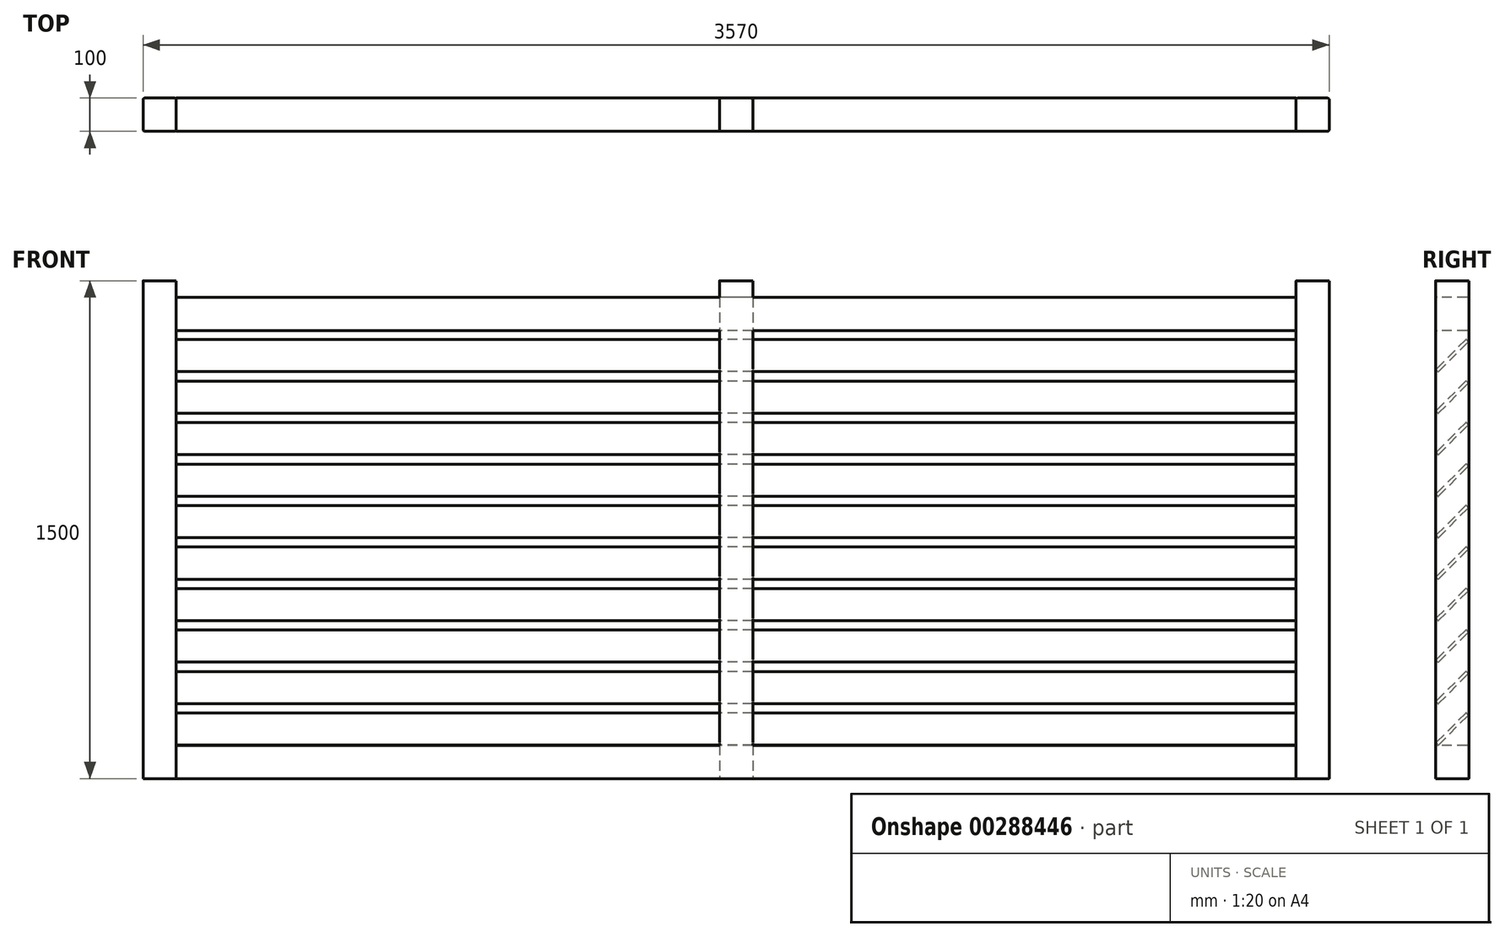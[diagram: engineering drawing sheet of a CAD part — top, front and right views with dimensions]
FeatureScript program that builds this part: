
annotation { "Feature Type Name" : "Feature", "Feature Type Description" : "" }
export const myFeature = defineFeature(function(context is Context, id is Id, definition is map)
    precondition{}
    {
        {
            var Q0;
            Q0=qCreatedBy(makeId("Right.planeOp"),FACE);
            var sketch = newSketch(context, id + "F0", { "sketchPlane" : qUnion([Q0])});
            skLineSegment(sketch, "E0", {"start": v(1.41, 1.41) * mm, "end": v(89.8, 89.8) * mm});
            skLineSegment(sketch, "E1", {"start": v(89.8, 92.63) * mm, "end": v(85.56, 96.87) * mm});
            skLineSegment(sketch, "E2", {"start": v(82.73, 96.87) * mm, "end": v(-5.66, 8.49) * mm});
            skLineSegment(sketch, "E3", {"start": v(-5.66, 5.66) * mm, "end": v(-1.41, 1.41) * mm});
            skPoint(sketch, "E4.visualSharp", {"position": v(84.15, 98.29) * mm});
            skArc(sketch, "E4.filletArc", {"start": v(85.56, 96.87) * mm, "mid": v(84.15, 97.46) * mm, "end": v(82.73, 96.87) * mm});
            skPoint(sketch, "E5.visualSharp", {"position": v(91.22, 91.22) * mm});
            skArc(sketch, "E5.filletArc", {"start": v(89.8, 89.8) * mm, "mid": v(90.39, 91.22) * mm, "end": v(89.8, 92.63) * mm});
            skPoint(sketch, "E6.visualSharp", {"position": v(0, 0) * mm});
            skArc(sketch, "E6.filletArc", {"start": v(-1.41, 1.41) * mm, "mid": v(0, 0.83) * mm, "end": v(1.41, 1.41) * mm});
            skPoint(sketch, "E7.visualSharp", {"position": v(-7.07, 7.07) * mm});
            skArc(sketch, "E7.filletArc", {"start": v(-5.66, 8.49) * mm, "mid": v(-6.24, 7.07) * mm, "end": v(-5.66, 5.66) * mm});
            skLineSegment(sketch, "E8.0.1.0", {"start": v(1.41, 126.41) * mm, "end": v(89.8, 214.8) * mm});
            skLineSegment(sketch, "E8.0.1.1", {"start": v(82.73, 221.87) * mm, "end": v(-5.66, 133.49) * mm});
            skPoint(sketch, "E8.0.1.2", {"position": v(84.15, 223.29) * mm});
            skPoint(sketch, "E8.0.1.3", {"position": v(91.22, 216.22) * mm});
            skPoint(sketch, "E8.0.1.4", {"position": v(-7.07, 132.07) * mm});
            skPoint(sketch, "E8.0.1.5", {"position": v(0, 125) * mm});
            skArc(sketch, "E8.0.1.6", {"start": v(89.8, 214.8) * mm, "mid": v(90.39, 216.22) * mm, "end": v(89.8, 217.63) * mm});
            skArc(sketch, "E8.0.1.7", {"start": v(-1.41, 126.41) * mm, "mid": v(0, 125.83) * mm, "end": v(1.41, 126.41) * mm});
            skArc(sketch, "E8.0.1.8", {"start": v(85.56, 221.87) * mm, "mid": v(84.15, 222.46) * mm, "end": v(82.73, 221.87) * mm});
            skLineSegment(sketch, "E8.0.1.9", {"start": v(-5.66, 130.66) * mm, "end": v(-1.41, 126.41) * mm});
            skArc(sketch, "E8.0.1.10", {"start": v(-5.66, 133.49) * mm, "mid": v(-6.24, 132.07) * mm, "end": v(-5.66, 130.66) * mm});
            skLineSegment(sketch, "E8.0.1.11", {"start": v(89.8, 217.63) * mm, "end": v(85.56, 221.87) * mm});
            skLineSegment(sketch, "E8.0.2.0", {"start": v(1.41, 251.41) * mm, "end": v(89.8, 339.8) * mm});
            skLineSegment(sketch, "E8.0.2.1", {"start": v(82.73, 346.87) * mm, "end": v(-5.66, 258.49) * mm});
            skPoint(sketch, "E8.0.2.2", {"position": v(84.15, 348.29) * mm});
            skPoint(sketch, "E8.0.2.3", {"position": v(91.22, 341.22) * mm});
            skPoint(sketch, "E8.0.2.4", {"position": v(-7.07, 257.07) * mm});
            skPoint(sketch, "E8.0.2.5", {"position": v(0, 250) * mm});
            skArc(sketch, "E8.0.2.6", {"start": v(89.8, 339.8) * mm, "mid": v(90.39, 341.22) * mm, "end": v(89.8, 342.63) * mm});
            skArc(sketch, "E8.0.2.7", {"start": v(-1.41, 251.41) * mm, "mid": v(0, 250.83) * mm, "end": v(1.41, 251.41) * mm});
            skArc(sketch, "E8.0.2.8", {"start": v(85.56, 346.87) * mm, "mid": v(84.15, 347.46) * mm, "end": v(82.73, 346.87) * mm});
            skLineSegment(sketch, "E8.0.2.9", {"start": v(-5.66, 255.66) * mm, "end": v(-1.41, 251.41) * mm});
            skArc(sketch, "E8.0.2.10", {"start": v(-5.66, 258.49) * mm, "mid": v(-6.24, 257.07) * mm, "end": v(-5.66, 255.66) * mm});
            skLineSegment(sketch, "E8.0.2.11", {"start": v(89.8, 342.63) * mm, "end": v(85.56, 346.87) * mm});
            skLineSegment(sketch, "E8.0.3.0", {"start": v(1.41, 376.41) * mm, "end": v(89.8, 464.8) * mm});
            skLineSegment(sketch, "E8.0.3.1", {"start": v(82.73, 471.87) * mm, "end": v(-5.66, 383.49) * mm});
            skPoint(sketch, "E8.0.3.2", {"position": v(84.15, 473.29) * mm});
            skPoint(sketch, "E8.0.3.3", {"position": v(91.22, 466.22) * mm});
            skPoint(sketch, "E8.0.3.4", {"position": v(-7.07, 382.07) * mm});
            skPoint(sketch, "E8.0.3.5", {"position": v(0, 375) * mm});
            skArc(sketch, "E8.0.3.6", {"start": v(89.8, 464.8) * mm, "mid": v(90.39, 466.22) * mm, "end": v(89.8, 467.63) * mm});
            skArc(sketch, "E8.0.3.7", {"start": v(-1.41, 376.41) * mm, "mid": v(0, 375.83) * mm, "end": v(1.41, 376.41) * mm});
            skArc(sketch, "E8.0.3.8", {"start": v(85.56, 471.87) * mm, "mid": v(84.15, 472.46) * mm, "end": v(82.73, 471.87) * mm});
            skLineSegment(sketch, "E8.0.3.9", {"start": v(-5.66, 380.66) * mm, "end": v(-1.41, 376.41) * mm});
            skArc(sketch, "E8.0.3.10", {"start": v(-5.66, 383.49) * mm, "mid": v(-6.24, 382.07) * mm, "end": v(-5.66, 380.66) * mm});
            skLineSegment(sketch, "E8.0.3.11", {"start": v(89.8, 467.63) * mm, "end": v(85.56, 471.87) * mm});
            skLineSegment(sketch, "E8.0.4.0", {"start": v(1.41, 501.41) * mm, "end": v(89.8, 589.8) * mm});
            skLineSegment(sketch, "E8.0.4.1", {"start": v(82.73, 596.87) * mm, "end": v(-5.66, 508.49) * mm});
            skPoint(sketch, "E8.0.4.2", {"position": v(84.15, 598.29) * mm});
            skPoint(sketch, "E8.0.4.3", {"position": v(91.22, 591.22) * mm});
            skPoint(sketch, "E8.0.4.4", {"position": v(-7.07, 507.07) * mm});
            skPoint(sketch, "E8.0.4.5", {"position": v(0, 500) * mm});
            skArc(sketch, "E8.0.4.6", {"start": v(89.8, 589.8) * mm, "mid": v(90.39, 591.22) * mm, "end": v(89.8, 592.63) * mm});
            skArc(sketch, "E8.0.4.7", {"start": v(-1.41, 501.41) * mm, "mid": v(0, 500.83) * mm, "end": v(1.41, 501.41) * mm});
            skArc(sketch, "E8.0.4.8", {"start": v(85.56, 596.87) * mm, "mid": v(84.15, 597.46) * mm, "end": v(82.73, 596.87) * mm});
            skLineSegment(sketch, "E8.0.4.9", {"start": v(-5.66, 505.66) * mm, "end": v(-1.41, 501.41) * mm});
            skArc(sketch, "E8.0.4.10", {"start": v(-5.66, 508.49) * mm, "mid": v(-6.24, 507.07) * mm, "end": v(-5.66, 505.66) * mm});
            skLineSegment(sketch, "E8.0.4.11", {"start": v(89.8, 592.63) * mm, "end": v(85.56, 596.87) * mm});
            skLineSegment(sketch, "E8.0.5.0", {"start": v(1.41, 626.41) * mm, "end": v(89.8, 714.8) * mm});
            skLineSegment(sketch, "E8.0.5.1", {"start": v(82.73, 721.87) * mm, "end": v(-5.66, 633.49) * mm});
            skPoint(sketch, "E8.0.5.2", {"position": v(84.15, 723.29) * mm});
            skPoint(sketch, "E8.0.5.3", {"position": v(91.22, 716.22) * mm});
            skPoint(sketch, "E8.0.5.4", {"position": v(-7.07, 632.07) * mm});
            skPoint(sketch, "E8.0.5.5", {"position": v(0, 625) * mm});
            skArc(sketch, "E8.0.5.6", {"start": v(89.8, 714.8) * mm, "mid": v(90.39, 716.22) * mm, "end": v(89.8, 717.63) * mm});
            skArc(sketch, "E8.0.5.7", {"start": v(-1.41, 626.41) * mm, "mid": v(0, 625.83) * mm, "end": v(1.41, 626.41) * mm});
            skArc(sketch, "E8.0.5.8", {"start": v(85.56, 721.87) * mm, "mid": v(84.15, 722.46) * mm, "end": v(82.73, 721.87) * mm});
            skLineSegment(sketch, "E8.0.5.9", {"start": v(-5.66, 630.66) * mm, "end": v(-1.41, 626.41) * mm});
            skArc(sketch, "E8.0.5.10", {"start": v(-5.66, 633.49) * mm, "mid": v(-6.24, 632.07) * mm, "end": v(-5.66, 630.66) * mm});
            skLineSegment(sketch, "E8.0.5.11", {"start": v(89.8, 717.63) * mm, "end": v(85.56, 721.87) * mm});
            skLineSegment(sketch, "E8.0.6.0", {"start": v(1.41, 751.41) * mm, "end": v(89.8, 839.8) * mm});
            skLineSegment(sketch, "E8.0.6.1", {"start": v(82.73, 846.87) * mm, "end": v(-5.66, 758.49) * mm});
            skPoint(sketch, "E8.0.6.2", {"position": v(84.15, 848.29) * mm});
            skPoint(sketch, "E8.0.6.3", {"position": v(91.22, 841.22) * mm});
            skPoint(sketch, "E8.0.6.4", {"position": v(-7.07, 757.07) * mm});
            skPoint(sketch, "E8.0.6.5", {"position": v(0, 750) * mm});
            skArc(sketch, "E8.0.6.6", {"start": v(89.8, 839.8) * mm, "mid": v(90.39, 841.22) * mm, "end": v(89.8, 842.63) * mm});
            skArc(sketch, "E8.0.6.7", {"start": v(-1.41, 751.41) * mm, "mid": v(0, 750.83) * mm, "end": v(1.41, 751.41) * mm});
            skArc(sketch, "E8.0.6.8", {"start": v(85.56, 846.87) * mm, "mid": v(84.15, 847.46) * mm, "end": v(82.73, 846.87) * mm});
            skLineSegment(sketch, "E8.0.6.9", {"start": v(-5.66, 755.66) * mm, "end": v(-1.41, 751.41) * mm});
            skArc(sketch, "E8.0.6.10", {"start": v(-5.66, 758.49) * mm, "mid": v(-6.24, 757.07) * mm, "end": v(-5.66, 755.66) * mm});
            skLineSegment(sketch, "E8.0.6.11", {"start": v(89.8, 842.63) * mm, "end": v(85.56, 846.87) * mm});
            skLineSegment(sketch, "E8.0.7.0", {"start": v(1.41, 876.41) * mm, "end": v(89.8, 964.8) * mm});
            skLineSegment(sketch, "E8.0.7.1", {"start": v(82.73, 971.87) * mm, "end": v(-5.66, 883.49) * mm});
            skPoint(sketch, "E8.0.7.2", {"position": v(84.15, 973.29) * mm});
            skPoint(sketch, "E8.0.7.3", {"position": v(91.22, 966.22) * mm});
            skPoint(sketch, "E8.0.7.4", {"position": v(-7.07, 882.07) * mm});
            skPoint(sketch, "E8.0.7.5", {"position": v(0, 875) * mm});
            skArc(sketch, "E8.0.7.6", {"start": v(89.8, 964.8) * mm, "mid": v(90.39, 966.22) * mm, "end": v(89.8, 967.63) * mm});
            skArc(sketch, "E8.0.7.7", {"start": v(-1.41, 876.41) * mm, "mid": v(0, 875.83) * mm, "end": v(1.41, 876.41) * mm});
            skArc(sketch, "E8.0.7.8", {"start": v(85.56, 971.87) * mm, "mid": v(84.15, 972.46) * mm, "end": v(82.73, 971.87) * mm});
            skLineSegment(sketch, "E8.0.7.9", {"start": v(-5.66, 880.66) * mm, "end": v(-1.41, 876.41) * mm});
            skArc(sketch, "E8.0.7.10", {"start": v(-5.66, 883.49) * mm, "mid": v(-6.24, 882.07) * mm, "end": v(-5.66, 880.66) * mm});
            skLineSegment(sketch, "E8.0.7.11", {"start": v(89.8, 967.63) * mm, "end": v(85.56, 971.87) * mm});
            skLineSegment(sketch, "E8.direction1", {"start": v(0, 0) * mm, "end": v(25, 0) * mm, "construction": true});
            skLineSegment(sketch, "E8.direction2", {"start": v(0, 0) * mm, "end": v(0, 125) * mm, "construction": true});
            skLineSegment(sketch, "E9.0.0.8", {"start": v(1.41, 1001.41) * mm, "end": v(89.8, 1089.8) * mm});
            skLineSegment(sketch, "E9.3.0.8", {"start": v(82.73, 1096.87) * mm, "end": v(-5.66, 1008.49) * mm});
            skPoint(sketch, "E9.6.0.8", {"position": v(84.15, 1098.29) * mm});
            skPoint(sketch, "E9.7.0.8", {"position": v(91.22, 1091.22) * mm});
            skPoint(sketch, "E9.8.0.8", {"position": v(-7.07, 1007.07) * mm});
            skPoint(sketch, "E9.9.0.8", {"position": v(0, 1000) * mm});
            skArc(sketch, "E9.10.0.8", {"start": v(89.8, 1089.8) * mm, "mid": v(90.39, 1091.22) * mm, "end": v(89.8, 1092.63) * mm});
            skArc(sketch, "E9.14.0.8", {"start": v(-1.41, 1001.41) * mm, "mid": v(0, 1000.83) * mm, "end": v(1.41, 1001.41) * mm});
            skArc(sketch, "E9.18.0.8", {"start": v(85.56, 1096.87) * mm, "mid": v(84.15, 1097.46) * mm, "end": v(82.73, 1096.87) * mm});
            skLineSegment(sketch, "E9.22.0.8", {"start": v(-5.66, 1005.66) * mm, "end": v(-1.41, 1001.41) * mm});
            skArc(sketch, "E9.25.0.8", {"start": v(-5.66, 1008.49) * mm, "mid": v(-6.24, 1007.07) * mm, "end": v(-5.66, 1005.66) * mm});
            skLineSegment(sketch, "E9.29.0.8", {"start": v(89.8, 1092.63) * mm, "end": v(85.56, 1096.87) * mm});
            skLineSegment(sketch, "E9.0.0.9", {"start": v(1.41, 1126.41) * mm, "end": v(89.8, 1214.8) * mm});
            skLineSegment(sketch, "E9.3.0.9", {"start": v(82.73, 1221.87) * mm, "end": v(-5.66, 1133.49) * mm});
            skPoint(sketch, "E9.6.0.9", {"position": v(84.15, 1223.29) * mm});
            skPoint(sketch, "E9.7.0.9", {"position": v(91.22, 1216.22) * mm});
            skPoint(sketch, "E9.8.0.9", {"position": v(-7.07, 1132.07) * mm});
            skPoint(sketch, "E9.9.0.9", {"position": v(0, 1125) * mm});
            skArc(sketch, "E9.10.0.9", {"start": v(89.8, 1214.8) * mm, "mid": v(90.39, 1216.22) * mm, "end": v(89.8, 1217.63) * mm});
            skArc(sketch, "E9.14.0.9", {"start": v(-1.41, 1126.41) * mm, "mid": v(0, 1125.83) * mm, "end": v(1.41, 1126.41) * mm});
            skArc(sketch, "E9.18.0.9", {"start": v(85.56, 1221.87) * mm, "mid": v(84.15, 1222.46) * mm, "end": v(82.73, 1221.87) * mm});
            skLineSegment(sketch, "E9.22.0.9", {"start": v(-5.66, 1130.66) * mm, "end": v(-1.41, 1126.41) * mm});
            skArc(sketch, "E9.25.0.9", {"start": v(-5.66, 1133.49) * mm, "mid": v(-6.24, 1132.07) * mm, "end": v(-5.66, 1130.66) * mm});
            skLineSegment(sketch, "E9.29.0.9", {"start": v(89.8, 1217.63) * mm, "end": v(85.56, 1221.87) * mm});
            skSolve(sketch);
        }
        {
            var Q0;
            Q0=makeQuery(id+"F0.imprint","IMPRINT",FACE,{"disambiguationData":[TD([[makeQuery(id+"F0.imprint","IMPRINT",EDGE,{"derivedFrom":sQuery(id+"F0.wireOp",EDGE,"E0")}),1.0]])]});
            var Q1;
            Q1=makeQuery(id+"F0.imprint","IMPRINT",FACE,{"disambiguationData":[TD([[makeQuery(id+"F0.imprint","IMPRINT",EDGE,{"derivedFrom":sQuery(id+"F0.wireOp",EDGE,"E8.0.1.0")}),1.0]])]});
            var Q2;
            Q2=makeQuery(id+"F0.imprint","IMPRINT",FACE,{"disambiguationData":[TD([[makeQuery(id+"F0.imprint","IMPRINT",EDGE,{"derivedFrom":sQuery(id+"F0.wireOp",EDGE,"E8.0.2.0")}),1.0]])]});
            var Q3;
            Q3=makeQuery(id+"F0.imprint","IMPRINT",FACE,{"disambiguationData":[TD([[makeQuery(id+"F0.imprint","IMPRINT",EDGE,{"derivedFrom":sQuery(id+"F0.wireOp",EDGE,"E8.0.3.0")}),1.0]])]});
            var Q4;
            Q4=makeQuery(id+"F0.imprint","IMPRINT",FACE,{"disambiguationData":[TD([[makeQuery(id+"F0.imprint","IMPRINT",EDGE,{"derivedFrom":sQuery(id+"F0.wireOp",EDGE,"E8.0.4.0")}),1.0]])]});
            var Q5;
            Q5=makeQuery(id+"F0.imprint","IMPRINT",FACE,{"disambiguationData":[TD([[makeQuery(id+"F0.imprint","IMPRINT",EDGE,{"derivedFrom":sQuery(id+"F0.wireOp",EDGE,"E8.0.5.0")}),1.0]])]});
            var Q6;
            Q6=makeQuery(id+"F0.imprint","IMPRINT",FACE,{"disambiguationData":[TD([[makeQuery(id+"F0.imprint","IMPRINT",EDGE,{"derivedFrom":sQuery(id+"F0.wireOp",EDGE,"E8.0.6.0")}),1.0]])]});
            var Q7;
            Q7=makeQuery(id+"F0.imprint","IMPRINT",FACE,{"disambiguationData":[TD([[makeQuery(id+"F0.imprint","IMPRINT",EDGE,{"derivedFrom":sQuery(id+"F0.wireOp",EDGE,"E8.0.7.0")}),1.0]])]});
            var Q8;
            Q8=makeQuery(id+"F0.imprint","IMPRINT",FACE,{"disambiguationData":[TD([[makeQuery(id+"F0.imprint","IMPRINT",EDGE,{"derivedFrom":sQuery(id+"F0.wireOp",EDGE,"E8.0.8.0")}),1.0]])]});
            var Q9;
            Q9=makeQuery(id+"F0.imprint","IMPRINT",FACE,{"disambiguationData":[TD([[makeQuery(id+"F0.imprint","IMPRINT",EDGE,{"derivedFrom":sQuery(id+"F0.wireOp",EDGE,"E8.0.9.0")}),1.0]])]});
            var Q10;
            Q10=makeQuery(id+"F0.imprint","IMPRINT",FACE,{"disambiguationData":[TD([[makeQuery(id+"F0.imprint","IMPRINT",EDGE,{"derivedFrom":sQuery(id+"F0.wireOp",EDGE,"E8.0.10.0")}),1.0]])]});
            var Q11;
            Q11=makeQuery(id+"F0.imprint","IMPRINT",FACE,{"disambiguationData":[TD([[makeQuery(id+"F0.imprint","IMPRINT",EDGE,{"derivedFrom":sQuery(id+"F0.wireOp",EDGE,"E8.0.28.0")}),1.0]])]});
            var Q12;
            Q12=makeQuery(id+"F0.imprint","IMPRINT",FACE,{"disambiguationData":[TD([[makeQuery(id+"F0.imprint","IMPRINT",EDGE,{"derivedFrom":sQuery(id+"F0.wireOp",EDGE,"E8.0.27.0")}),1.0]])]});
            var Q13;
            Q13=makeQuery(id+"F0.imprint","IMPRINT",FACE,{"disambiguationData":[TD([[makeQuery(id+"F0.imprint","IMPRINT",EDGE,{"derivedFrom":sQuery(id+"F0.wireOp",EDGE,"E8.0.26.0")}),1.0]])]});
            var Q14;
            Q14=makeQuery(id+"F0.imprint","IMPRINT",FACE,{"disambiguationData":[TD([[makeQuery(id+"F0.imprint","IMPRINT",EDGE,{"derivedFrom":sQuery(id+"F0.wireOp",EDGE,"E8.0.29.0")}),1.0]])]});
            var Q15;
            Q15=makeQuery(id+"F0.imprint","IMPRINT",FACE,{"disambiguationData":[TD([[makeQuery(id+"F0.imprint","IMPRINT",EDGE,{"derivedFrom":sQuery(id+"F0.wireOp",EDGE,"E8.0.16.0")}),1.0]])]});
            var Q16;
            Q16=makeQuery(id+"F0.imprint","IMPRINT",FACE,{"disambiguationData":[TD([[makeQuery(id+"F0.imprint","IMPRINT",EDGE,{"derivedFrom":sQuery(id+"F0.wireOp",EDGE,"E8.0.17.0")}),1.0]])]});
            var Q17;
            Q17=makeQuery(id+"F0.imprint","IMPRINT",FACE,{"disambiguationData":[TD([[makeQuery(id+"F0.imprint","IMPRINT",EDGE,{"derivedFrom":sQuery(id+"F0.wireOp",EDGE,"E8.0.18.0")}),1.0]])]});
            var Q18;
            Q18=makeQuery(id+"F0.imprint","IMPRINT",FACE,{"disambiguationData":[TD([[makeQuery(id+"F0.imprint","IMPRINT",EDGE,{"derivedFrom":sQuery(id+"F0.wireOp",EDGE,"E8.0.19.0")}),1.0]])]});
            var Q19;
            Q19=makeQuery(id+"F0.imprint","IMPRINT",FACE,{"disambiguationData":[TD([[makeQuery(id+"F0.imprint","IMPRINT",EDGE,{"derivedFrom":sQuery(id+"F0.wireOp",EDGE,"E8.0.20.0")}),1.0]])]});
            var Q20;
            Q20=makeQuery(id+"F0.imprint","IMPRINT",FACE,{"disambiguationData":[TD([[makeQuery(id+"F0.imprint","IMPRINT",EDGE,{"derivedFrom":sQuery(id+"F0.wireOp",EDGE,"E8.0.21.0")}),1.0]])]});
            var Q21;
            Q21=makeQuery(id+"F0.imprint","IMPRINT",FACE,{"disambiguationData":[TD([[makeQuery(id+"F0.imprint","IMPRINT",EDGE,{"derivedFrom":sQuery(id+"F0.wireOp",EDGE,"E8.0.22.0")}),1.0]])]});
            var Q22;
            Q22=makeQuery(id+"F0.imprint","IMPRINT",FACE,{"disambiguationData":[TD([[makeQuery(id+"F0.imprint","IMPRINT",EDGE,{"derivedFrom":sQuery(id+"F0.wireOp",EDGE,"E8.0.15.0")}),1.0]])]});
            var Q23;
            Q23=makeQuery(id+"F0.imprint","IMPRINT",FACE,{"disambiguationData":[TD([[makeQuery(id+"F0.imprint","IMPRINT",EDGE,{"derivedFrom":sQuery(id+"F0.wireOp",EDGE,"E8.0.13.0")}),1.0]])]});
            var Q24;
            Q24=makeQuery(id+"F0.imprint","IMPRINT",FACE,{"disambiguationData":[TD([[makeQuery(id+"F0.imprint","IMPRINT",EDGE,{"derivedFrom":sQuery(id+"F0.wireOp",EDGE,"E8.0.14.0")}),1.0]])]});
            var Q25;
            Q25=makeQuery(id+"F0.imprint","IMPRINT",FACE,{"disambiguationData":[TD([[makeQuery(id+"F0.imprint","IMPRINT",EDGE,{"derivedFrom":sQuery(id+"F0.wireOp",EDGE,"E8.0.11.0")}),1.0]])]});
            var Q26;
            Q26=makeQuery(id+"F0.imprint","IMPRINT",FACE,{"disambiguationData":[TD([[makeQuery(id+"F0.imprint","IMPRINT",EDGE,{"derivedFrom":sQuery(id+"F0.wireOp",EDGE,"E8.0.12.0")}),1.0]])]});
            var Q27;
            Q27=makeQuery(id+"F0.imprint","IMPRINT",FACE,{"disambiguationData":[TD([[makeQuery(id+"F0.imprint","IMPRINT",EDGE,{"derivedFrom":sQuery(id+"F0.wireOp",EDGE,"E8.0.23.0")}),1.0]])]});
            var Q28;
            Q28=makeQuery(id+"F0.imprint","IMPRINT",FACE,{"disambiguationData":[TD([[makeQuery(id+"F0.imprint","IMPRINT",EDGE,{"derivedFrom":sQuery(id+"F0.wireOp",EDGE,"E8.0.24.0")}),1.0]])]});
            var Q29;
            Q29=makeQuery(id+"F0.imprint","IMPRINT",FACE,{"disambiguationData":[TD([[makeQuery(id+"F0.imprint","IMPRINT",EDGE,{"derivedFrom":sQuery(id+"F0.wireOp",EDGE,"E8.0.25.0")}),1.0]])]});
            var Q30;
            Q30=makeQuery(id+"F0.imprint","IMPRINT",FACE,{"disambiguationData":[TD([[makeQuery(id+"F0.imprint","IMPRINT",EDGE,{"derivedFrom":sQuery(id+"F0.wireOp",EDGE,"E9.0.0.8")}),1.0]])]});
            var Q31;
            Q31=makeQuery(id+"F0.imprint","IMPRINT",FACE,{"disambiguationData":[TD([[makeQuery(id+"F0.imprint","IMPRINT",EDGE,{"derivedFrom":sQuery(id+"F0.wireOp",EDGE,"E9.0.0.9")}),1.0]])]});
            var Q32;
            Q32=makeQuery(id+"F0.imprint","IMPRINT",FACE,{"disambiguationData":[TD([[makeQuery(id+"F0.imprint","IMPRINT",EDGE,{"derivedFrom":sQuery(id+"F0.wireOp",EDGE,"E9.0.0.10")}),1.0]])]});
            var Q33;
            Q33=makeQuery(id+"F0.imprint","IMPRINT",FACE,{"disambiguationData":[TD([[makeQuery(id+"F0.imprint","IMPRINT",EDGE,{"derivedFrom":sQuery(id+"F0.wireOp",EDGE,"E9.0.0.11")}),1.0]])]});
            extrude(context, id + "F1", {"entities" : qUnion([Q0, Q1, Q2, Q3, Q4, Q5, Q6, Q7, Q8, Q9, Q10, Q11, Q12, Q13, Q14, Q15, Q16, Q17, Q18, Q19, Q20, Q21, Q22, Q23, Q24, Q25, Q26, Q27, Q28, Q29, Q30, Q31, Q32, Q33]), "depth" : 3370 * mm});
        }
        {
            var Q0;
            Q0=qCreatedBy(makeId("Top.planeOp"),FACE);
            var sketch = newSketch(context, id + "F2", { "sketchPlane" : qUnion([Q0])});
            skLineSegment(sketch, "E10.bottom", {"start": v(-5, -8) * mm, "end": v(-95, -8) * mm});
            skLineSegment(sketch, "E10.top", {"start": v(-5, 92) * mm, "end": v(-95, 92) * mm});
            skLineSegment(sketch, "E10.left", {"start": v(0, -3) * mm, "end": v(0, 87) * mm});
            skLineSegment(sketch, "E10.right", {"start": v(-100, -3) * mm, "end": v(-100, 87) * mm});
            skPoint(sketch, "E11.visualSharp", {"position": v(-100, 92) * mm});
            skArc(sketch, "E11.filletArc", {"start": v(-95, 92) * mm, "mid": v(-98.54, 90.54) * mm, "end": v(-100, 87) * mm});
            skPoint(sketch, "E12.visualSharp", {"position": v(0, 92) * mm});
            skArc(sketch, "E12.filletArc", {"start": v(0, 87) * mm, "mid": v(-1.46, 90.54) * mm, "end": v(-5, 92) * mm});
            skPoint(sketch, "E13.visualSharp", {"position": v(0, -8) * mm});
            skArc(sketch, "E13.filletArc", {"start": v(-5, -8) * mm, "mid": v(-1.46, -6.54) * mm, "end": v(0, -3) * mm});
            skPoint(sketch, "E14.visualSharp", {"position": v(-100, -8) * mm});
            skArc(sketch, "E14.filletArc", {"start": v(-100, -3) * mm, "mid": v(-98.54, -6.54) * mm, "end": v(-95, -8) * mm});
            skLineSegment(sketch, "E15.1.0.0", {"start": v(1635, -3) * mm, "end": v(1635, 87) * mm});
            skLineSegment(sketch, "E15.1.0.1", {"start": v(1735, -3) * mm, "end": v(1735, 87) * mm});
            skLineSegment(sketch, "E15.1.0.2", {"start": v(1730, -8) * mm, "end": v(1640, -8) * mm});
            skLineSegment(sketch, "E15.1.0.3", {"start": v(1730, 92) * mm, "end": v(1640, 92) * mm});
            skPoint(sketch, "E15.1.0.4", {"position": v(1635, 92) * mm});
            skPoint(sketch, "E15.1.0.5", {"position": v(1635, -8) * mm});
            skPoint(sketch, "E15.1.0.6", {"position": v(1735, 92) * mm});
            skPoint(sketch, "E15.1.0.7", {"position": v(1735, -8) * mm});
            skArc(sketch, "E15.1.0.8", {"start": v(1635, -3) * mm, "mid": v(1636.46, -6.54) * mm, "end": v(1640, -8) * mm});
            skArc(sketch, "E15.1.0.9", {"start": v(1735, 87) * mm, "mid": v(1733.54, 90.54) * mm, "end": v(1730, 92) * mm});
            skArc(sketch, "E15.1.0.10", {"start": v(1730, -8) * mm, "mid": v(1733.54, -6.54) * mm, "end": v(1735, -3) * mm});
            skArc(sketch, "E15.1.0.11", {"start": v(1640, 92) * mm, "mid": v(1636.46, 90.54) * mm, "end": v(1635, 87) * mm});
            skLineSegment(sketch, "E15.direction1", {"start": v(-100, -8) * mm, "end": v(1635, -8) * mm, "construction": true});
            skLineSegment(sketch, "E16.0.2.0", {"start": v(3370, -3) * mm, "end": v(3370, 87) * mm});
            skLineSegment(sketch, "E16.3.2.0", {"start": v(3470, -3) * mm, "end": v(3470, 87) * mm});
            skLineSegment(sketch, "E16.6.2.0", {"start": v(3465, -8) * mm, "end": v(3375, -8) * mm});
            skLineSegment(sketch, "E16.9.2.0", {"start": v(3465, 92) * mm, "end": v(3375, 92) * mm});
            skPoint(sketch, "E16.12.2.0", {"position": v(3370, 92) * mm});
            skPoint(sketch, "E16.13.2.0", {"position": v(3370, -8) * mm});
            skPoint(sketch, "E16.14.2.0", {"position": v(3470, 92) * mm});
            skPoint(sketch, "E16.15.2.0", {"position": v(3470, -8) * mm});
            skArc(sketch, "E16.16.2.0", {"start": v(3370, -3) * mm, "mid": v(3371.46, -6.54) * mm, "end": v(3375, -8) * mm});
            skArc(sketch, "E16.20.2.0", {"start": v(3470, 87) * mm, "mid": v(3468.54, 90.54) * mm, "end": v(3465, 92) * mm});
            skArc(sketch, "E16.24.2.0", {"start": v(3465, -8) * mm, "mid": v(3468.54, -6.54) * mm, "end": v(3470, -3) * mm});
            skArc(sketch, "E16.28.2.0", {"start": v(3375, 92) * mm, "mid": v(3371.46, 90.54) * mm, "end": v(3370, 87) * mm});
            skSolve(sketch);
        }
        {
            var Q0;
            Q0=makeQuery(id+"F2.imprint","IMPRINT",FACE,{"disambiguationData":[TD([[makeQuery(id+"F2.imprint","IMPRINT",EDGE,{"derivedFrom":sQuery(id+"F2.wireOp",EDGE,"E10.bottom")}),-1.0]])]});
            var Q1;
            Q1=makeQuery(id+"F2.imprint","IMPRINT",FACE,{"disambiguationData":[TD([[makeQuery(id+"F2.imprint","IMPRINT",EDGE,{"derivedFrom":sQuery(id+"F2.wireOp",EDGE,"E15.1.0.0")}),-1.0]])]});
            var Q2;
            Q2=makeQuery(id+"F2.imprint","IMPRINT",FACE,{"disambiguationData":[TD([[makeQuery(id+"F2.imprint","IMPRINT",EDGE,{"derivedFrom":sQuery(id+"F2.wireOp",EDGE,"E16.0.2.0")}),-1.0]])]});
            extrude(context, id + "F3", {"entities" : qUnion([Q0, Q1, Q2]), "depth" : 1400 * mm, "hasSecondDirection" : true, "secondDirectionOppositeDirection" : true, "secondDirectionDepth" : 100 * mm});
        }
        {
            var Q0;
            Q0=makeQuery(id+"F3.opExtrude","SWEPT_FACE",FACE,{"disambiguationData":[OSD([sQuery(id+"F2.wireOp",EDGE,"E10.left")])]});
            var sketch = newSketch(context, id + "F4", { "sketchPlane" : qUnion([Q0])});
            skLineSegment(sketch, "E17.bottom", {"start": v(87, -100) * mm, "end": v(-3, -100) * mm});
            skLineSegment(sketch, "E17.top", {"start": v(87, 0) * mm, "end": v(-3, 0) * mm});
            skLineSegment(sketch, "E17.left", {"start": v(92, -95) * mm, "end": v(92, -5) * mm});
            skLineSegment(sketch, "E17.right", {"start": v(-8, -95) * mm, "end": v(-8, -5) * mm});
            skPoint(sketch, "E18.visualSharp", {"position": v(92, 0) * mm});
            skArc(sketch, "E18.filletArc", {"start": v(92, -5) * mm, "mid": v(90.54, -1.46) * mm, "end": v(87, 0) * mm});
            skPoint(sketch, "E19.visualSharp", {"position": v(92, -100) * mm});
            skArc(sketch, "E19.filletArc", {"start": v(87, -100) * mm, "mid": v(90.54, -98.54) * mm, "end": v(92, -95) * mm});
            skPoint(sketch, "E20.visualSharp", {"position": v(-8, -100) * mm});
            skArc(sketch, "E20.filletArc", {"start": v(-8, -95) * mm, "mid": v(-6.54, -98.54) * mm, "end": v(-3, -100) * mm});
            skPoint(sketch, "E21.visualSharp", {"position": v(-8, 0) * mm});
            skArc(sketch, "E21.filletArc", {"start": v(-3, 0) * mm, "mid": v(-6.54, -1.46) * mm, "end": v(-8, -5) * mm});
            skLineSegment(sketch, "E22.0.1.0", {"start": v(87, 1250) * mm, "end": v(-3, 1250) * mm});
            skPoint(sketch, "E22.0.1.1", {"position": v(-8, 1250) * mm});
            skPoint(sketch, "E22.0.1.2", {"position": v(-8, 1350) * mm});
            skLineSegment(sketch, "E22.0.1.3", {"start": v(-8, 1255) * mm, "end": v(-8, 1345) * mm});
            skPoint(sketch, "E22.0.1.4", {"position": v(92, 1350) * mm});
            skPoint(sketch, "E22.0.1.5", {"position": v(92, 1250) * mm});
            skLineSegment(sketch, "E22.0.1.6", {"start": v(92, 1255) * mm, "end": v(92, 1345) * mm});
            skLineSegment(sketch, "E22.0.1.7", {"start": v(87, 1350) * mm, "end": v(-3, 1350) * mm});
            skArc(sketch, "E22.0.1.8", {"start": v(-3, 1350) * mm, "mid": v(-6.54, 1348.54) * mm, "end": v(-8, 1345) * mm});
            skArc(sketch, "E22.0.1.9", {"start": v(-8, 1255) * mm, "mid": v(-6.54, 1251.46) * mm, "end": v(-3, 1250) * mm});
            skArc(sketch, "E22.0.1.10", {"start": v(87, 1250) * mm, "mid": v(90.54, 1251.46) * mm, "end": v(92, 1255) * mm});
            skArc(sketch, "E22.0.1.11", {"start": v(92, 1345) * mm, "mid": v(90.54, 1348.54) * mm, "end": v(87, 1350) * mm});
            skLineSegment(sketch, "E22.direction1", {"start": v(-8, -100) * mm, "end": v(17, -100) * mm, "construction": true});
            skLineSegment(sketch, "E22.direction2", {"start": v(-8, -100) * mm, "end": v(-8, 1250) * mm, "construction": true});
            skSolve(sketch);
        }
        {
            var Q0;
            {var subQ0=sQuery(id+"F4.wireOp",EDGE,"E22.0.1.0");Q0=makeQuery(id+"F4.imprint","IMPRINT",FACE,{"disambiguationData":[TD([[makeQuery(id+"F4.imprint","IMPRINT",EDGE,{"derivedFrom":subQ0}),-1.0]])]});}
            var Q1;
            {var subQ0=sQuery(id+"F4.wireOp",EDGE,"E17.bottom");Q1=makeQuery(id+"F4.imprint","IMPRINT",FACE,{"disambiguationData":[TD([[makeQuery(id+"F4.imprint","IMPRINT",EDGE,{"derivedFrom":subQ0}),1.0]])]});}
            var Q2;
            Q2=makeQuery(id+"F4.imprint","IMPRINT",FACE,{"disambiguationData":[TD([[makeQuery(id+"F4.imprint","IMPRINT",EDGE,{"derivedFrom":sQuery(id+"F4.wireOp",EDGE,"E17.left")}),1.0]])]});
            var Q3;
            Q3=makeQuery(id+"F4.imprint","IMPRINT",FACE,{"disambiguationData":[TD([[makeQuery(id+"F4.imprint","IMPRINT",EDGE,{"derivedFrom":sQuery(id+"F4.wireOp",EDGE,"E22.0.1.6")}),1.0]])]});
            var Q4;
            Q4=makeQuery(id+"F4.imprint","IMPRINT",FACE,{"disambiguationData":[TD([[makeQuery(id+"F4.imprint","IMPRINT",EDGE,{"derivedFrom":sQuery(id+"F4.wireOp",EDGE,"E22.0.1.3")}),-1.0]])]});
            var Q5;
            Q5=makeQuery(id+"F4.imprint","IMPRINT",FACE,{"disambiguationData":[TD([[makeQuery(id+"F4.imprint","IMPRINT",EDGE,{"derivedFrom":sQuery(id+"F4.wireOp",EDGE,"E17.right")}),-1.0]])]});
            extrude(context, id + "F5", {"entities" : qUnion([Q0, Q1, Q2, Q3, Q4, Q5]), "depth" : 3370 * mm});
        }
    });
